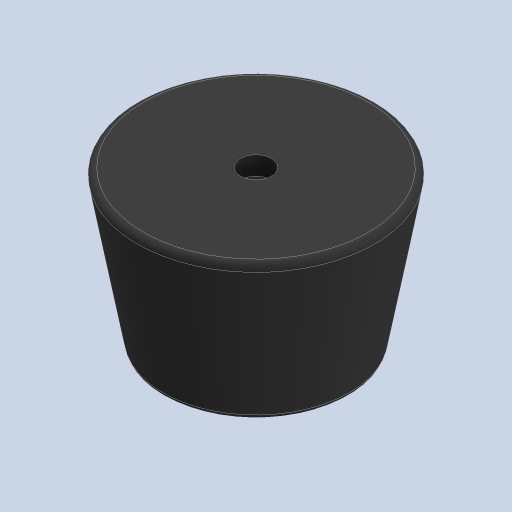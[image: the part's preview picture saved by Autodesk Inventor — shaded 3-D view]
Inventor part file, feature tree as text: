
AUTODESK INVENTOR PART (.ipt)
format: ipt  version: 2023 (Build 270158000, 158)  size: 180,224 bytes
history: native  units: mm
features: revolve x1, sketch x1
ambient origin geometry x8: Origin, YZ Plane, XZ Plane, XY Plane, X Axis, Y Axis, Z Axis, Center Point
bodies: Body1 (feature_tree)
feature tree (2):
  revolve  "Revolution1"  [1 undecoded]
  sketch  "Sketch5"  dims[d21=17.0mm d22=12.0mm d23=15.0mm d24=13.0mm d25=2.5mm d26=25.0mm d27=3.0mm d28=1.0mm d29=1.0mm d30=90.0deg]
note: 1 required parameter value undecoded (feature->parameter linkage not recoverable at this tier; creation-order binding heuristic only, values carry confidence <= 0.55)
